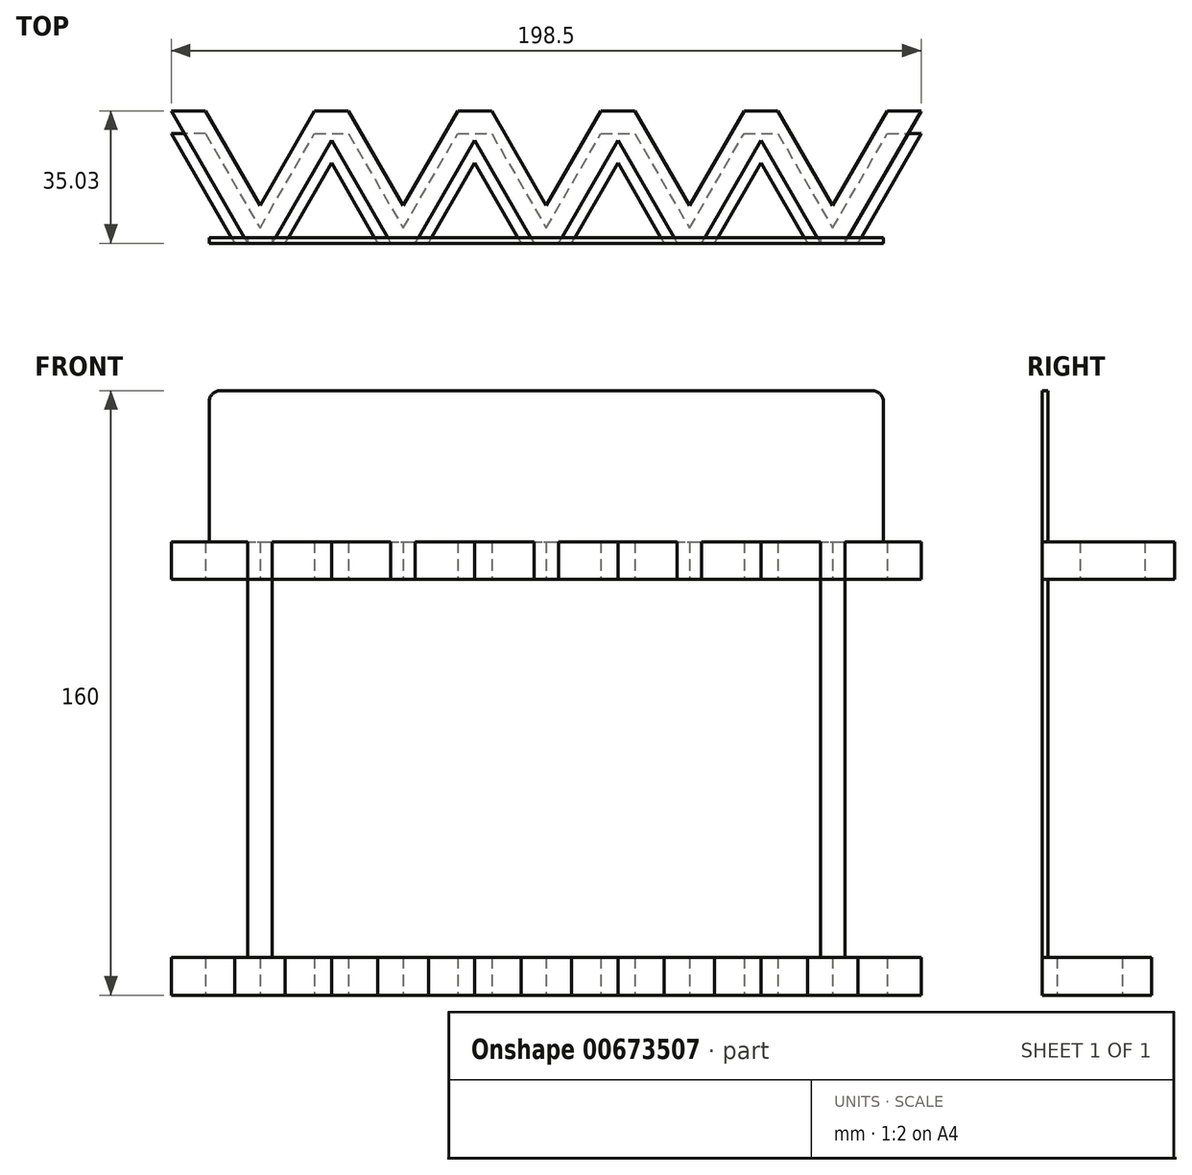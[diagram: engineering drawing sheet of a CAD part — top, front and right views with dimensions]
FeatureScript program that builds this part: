
annotation { "Feature Type Name" : "Feature", "Feature Type Description" : "" }
export const myFeature = defineFeature(function(context is Context, id is Id, definition is map)
    precondition{}
    {
        {
            var Q0;
            Q0=qCreatedBy(makeId("Top.planeOp"),FACE);
            var sketch = newSketch(context, id + "F0", { "sketchPlane" : qUnion([Q0])});
            skLineSegment(sketch, "E0", {"start": v(-76.95, 35.03) * mm, "end": v(-56.72, 0) * mm});
            skLineSegment(sketch, "E1", {"start": v(-50.27, 0) * mm, "end": v(-30.05, 35.03) * mm});
            skLineSegment(sketch, "E2", {"start": v(-67.95, 35.03) * mm, "end": v(-53.5, 10) * mm});
            skLineSegment(sketch, "E3", {"start": v(-53.5, 10) * mm, "end": v(-39.05, 35.03) * mm});
            skLineSegment(sketch, "E4", {"start": v(-76.95, 35.03) * mm, "end": v(-67.95, 35.03) * mm});
            skLineSegment(sketch, "E5", {"start": v(-56.72, 0) * mm, "end": v(-50.27, 0) * mm});
            skLineSegment(sketch, "E6", {"start": v(-39.05, 35.03) * mm, "end": v(-30.05, 35.03) * mm});
            skLineSegment(sketch, "E7.1.0.1", {"start": v(-39.05, 35.03) * mm, "end": v(-18.82, 0) * mm});
            skLineSegment(sketch, "E7.1.0.2", {"start": v(-30.05, 35.03) * mm, "end": v(-15.6, 10) * mm});
            skLineSegment(sketch, "E7.1.0.3", {"start": v(-15.6, 10) * mm, "end": v(-1.15, 35.03) * mm});
            skLineSegment(sketch, "E7.1.0.4", {"start": v(-1.15, 35.03) * mm, "end": v(7.85, 35.03) * mm});
            skLineSegment(sketch, "E7.1.0.5", {"start": v(-12.37, 0) * mm, "end": v(7.85, 35.03) * mm});
            skLineSegment(sketch, "E7.1.0.6", {"start": v(-18.82, 0) * mm, "end": v(-12.37, 0) * mm});
            skLineSegment(sketch, "E7.2.0.0", {"start": v(-1.15, 35.03) * mm, "end": v(7.85, 35.03) * mm});
            skLineSegment(sketch, "E7.2.0.1", {"start": v(-1.15, 35.03) * mm, "end": v(19.08, 0) * mm});
            skLineSegment(sketch, "E7.2.0.2", {"start": v(7.85, 35.03) * mm, "end": v(22.3, 10) * mm});
            skLineSegment(sketch, "E7.2.0.3", {"start": v(22.3, 10) * mm, "end": v(36.75, 35.03) * mm});
            skLineSegment(sketch, "E7.2.0.4", {"start": v(36.75, 35.03) * mm, "end": v(45.75, 35.03) * mm});
            skLineSegment(sketch, "E7.2.0.5", {"start": v(25.53, 0) * mm, "end": v(45.75, 35.03) * mm});
            skLineSegment(sketch, "E7.2.0.6", {"start": v(19.08, 0) * mm, "end": v(25.53, 0) * mm});
            skLineSegment(sketch, "E7.3.0.0", {"start": v(36.75, 35.03) * mm, "end": v(45.75, 35.03) * mm});
            skLineSegment(sketch, "E7.3.0.1", {"start": v(36.75, 35.03) * mm, "end": v(56.98, 0) * mm});
            skLineSegment(sketch, "E7.3.0.2", {"start": v(45.75, 35.03) * mm, "end": v(60.2, 10) * mm});
            skLineSegment(sketch, "E7.3.0.3", {"start": v(60.2, 10) * mm, "end": v(74.65, 35.03) * mm});
            skLineSegment(sketch, "E7.3.0.4", {"start": v(74.65, 35.03) * mm, "end": v(83.65, 35.03) * mm});
            skLineSegment(sketch, "E7.3.0.5", {"start": v(63.43, 0) * mm, "end": v(83.65, 35.03) * mm});
            skLineSegment(sketch, "E7.3.0.6", {"start": v(56.98, 0) * mm, "end": v(63.43, 0) * mm});
            skLineSegment(sketch, "E7.4.0.0", {"start": v(74.65, 35.03) * mm, "end": v(83.65, 35.03) * mm});
            skLineSegment(sketch, "E7.4.0.1", {"start": v(74.65, 35.03) * mm, "end": v(94.88, 0) * mm});
            skLineSegment(sketch, "E7.4.0.2", {"start": v(83.65, 35.03) * mm, "end": v(98.1, 10) * mm});
            skLineSegment(sketch, "E7.4.0.3", {"start": v(98.1, 10) * mm, "end": v(112.55, 35.03) * mm});
            skLineSegment(sketch, "E7.4.0.4", {"start": v(112.55, 35.03) * mm, "end": v(121.55, 35.03) * mm});
            skLineSegment(sketch, "E7.4.0.5", {"start": v(101.33, 0) * mm, "end": v(121.55, 35.03) * mm});
            skLineSegment(sketch, "E7.4.0.6", {"start": v(94.88, 0) * mm, "end": v(101.33, 0) * mm});
            skLineSegment(sketch, "E7.direction1", {"start": v(-76.95, 35.03) * mm, "end": v(-39.05, 35.03) * mm, "construction": true});
            skSolve(sketch);
        }
        {
            var Q0;
            Q0 = qSketchRegion(id + "F0", true);
            extrude(context, id + "F1", {"entities" : qUnion([Q0]), "endBound" : BoundingType.SYMMETRIC, "depth" : 10 * mm, "offsetDistance" : 25 * mm});
        }
        {
            var Q0;
            Q0=qCreatedBy(makeId("Top.planeOp"),FACE);
            cPlane(context, id + "F2", {"entities" : qUnion([Q0]), "cplaneType" : CPlaneType.OFFSET, "offset" : 110 * mm, "oppositeDirection" : true, "width" : 150 * mm, "height" : 150 * mm});
        }
        {
            var Q0;
            Q0=qCreatedBy(id+"F2.planeOp",FACE);
            var sketch = newSketch(context, id + "F3", { "sketchPlane" : qUnion([Q0])});
            skLineSegment(sketch, "E8", {"start": v(-76.95, 29.03) * mm, "end": v(-60.19, 0) * mm});
            skLineSegment(sketch, "E9", {"start": v(-46.8, 0) * mm, "end": v(-30.05, 29.03) * mm});
            skLineSegment(sketch, "E10", {"start": v(-67.95, 29.03) * mm, "end": v(-53.5, 4) * mm});
            skLineSegment(sketch, "E11", {"start": v(-53.5, 4) * mm, "end": v(-39.05, 29.03) * mm});
            skLineSegment(sketch, "E12.1.0.0", {"start": v(-39.05, 29.03) * mm, "end": v(-30.05, 29.03) * mm});
            skLineSegment(sketch, "E13", {"start": v(-67.95, 29.03) * mm, "end": v(-76.95, 29.03) * mm});
            skLineSegment(sketch, "E14", {"start": v(-46.8, 0) * mm, "end": v(-60.19, 0) * mm});
            skLineSegment(sketch, "E15.1.0.0", {"start": v(-1.15, 29.03) * mm, "end": v(7.85, 29.03) * mm});
            skLineSegment(sketch, "E15.1.0.1", {"start": v(-8.9, 0) * mm, "end": v(7.85, 29.03) * mm});
            skLineSegment(sketch, "E15.1.0.2", {"start": v(-15.6, 4) * mm, "end": v(-1.15, 29.03) * mm});
            skLineSegment(sketch, "E15.1.0.3", {"start": v(-8.9, 0) * mm, "end": v(-22.29, 0) * mm});
            skLineSegment(sketch, "E15.1.0.4", {"start": v(-39.05, 29.03) * mm, "end": v(-22.29, 0) * mm});
            skLineSegment(sketch, "E15.1.0.5", {"start": v(-30.05, 29.03) * mm, "end": v(-15.6, 4) * mm});
            skLineSegment(sketch, "E15.1.0.6", {"start": v(-30.05, 29.03) * mm, "end": v(-39.05, 29.03) * mm});
            skLineSegment(sketch, "E15.2.0.0", {"start": v(36.75, 29.03) * mm, "end": v(45.75, 29.03) * mm});
            skLineSegment(sketch, "E15.2.0.1", {"start": v(29, 0) * mm, "end": v(45.75, 29.03) * mm});
            skLineSegment(sketch, "E15.2.0.2", {"start": v(22.3, 4) * mm, "end": v(36.75, 29.03) * mm});
            skLineSegment(sketch, "E15.2.0.3", {"start": v(29, 0) * mm, "end": v(15.61, 0) * mm});
            skLineSegment(sketch, "E15.2.0.4", {"start": v(-1.15, 29.03) * mm, "end": v(15.61, 0) * mm});
            skLineSegment(sketch, "E15.2.0.5", {"start": v(7.85, 29.03) * mm, "end": v(22.3, 4) * mm});
            skLineSegment(sketch, "E15.2.0.6", {"start": v(7.85, 29.03) * mm, "end": v(-1.15, 29.03) * mm});
            skLineSegment(sketch, "E15.3.0.0", {"start": v(74.65, 29.03) * mm, "end": v(83.65, 29.03) * mm});
            skLineSegment(sketch, "E15.3.0.1", {"start": v(66.9, 0) * mm, "end": v(83.65, 29.03) * mm});
            skLineSegment(sketch, "E15.3.0.2", {"start": v(60.2, 4) * mm, "end": v(74.65, 29.03) * mm});
            skLineSegment(sketch, "E15.3.0.3", {"start": v(66.9, 0) * mm, "end": v(53.51, 0) * mm});
            skLineSegment(sketch, "E15.3.0.4", {"start": v(36.75, 29.03) * mm, "end": v(53.51, 0) * mm});
            skLineSegment(sketch, "E15.3.0.5", {"start": v(45.75, 29.03) * mm, "end": v(60.2, 4) * mm});
            skLineSegment(sketch, "E15.3.0.6", {"start": v(45.75, 29.03) * mm, "end": v(36.75, 29.03) * mm});
            skLineSegment(sketch, "E15.4.0.0", {"start": v(112.55, 29.03) * mm, "end": v(121.55, 29.03) * mm});
            skLineSegment(sketch, "E15.4.0.1", {"start": v(104.8, 0) * mm, "end": v(121.55, 29.03) * mm});
            skLineSegment(sketch, "E15.4.0.2", {"start": v(98.1, 4) * mm, "end": v(112.55, 29.03) * mm});
            skLineSegment(sketch, "E15.4.0.3", {"start": v(104.8, 0) * mm, "end": v(91.41, 0) * mm});
            skLineSegment(sketch, "E15.4.0.4", {"start": v(74.65, 29.03) * mm, "end": v(91.41, 0) * mm});
            skLineSegment(sketch, "E15.4.0.5", {"start": v(83.65, 29.03) * mm, "end": v(98.1, 4) * mm});
            skLineSegment(sketch, "E15.4.0.6", {"start": v(83.65, 29.03) * mm, "end": v(74.65, 29.03) * mm});
            skLineSegment(sketch, "E15.direction1", {"start": v(-39.05, 29.03) * mm, "end": v(-1.15, 29.03) * mm, "construction": true});
            skSolve(sketch);
        }
        {
            var Q0;
            Q0 = qSketchRegion(id + "F3", true);
            extrude(context, id + "F4", {"entities" : qUnion([Q0]), "endBound" : BoundingType.SYMMETRIC, "depth" : 10 * mm, "offsetDistance" : 25 * mm});
        }
        {
            var Q0;
            Q0=qCreatedBy(makeId("Front.planeOp"),FACE);
            var sketch = newSketch(context, id + "F5", { "sketchPlane" : qUnion([Q0])});
            skLineSegment(sketch, "E16.bottom", {"start": v(-63.95, 45) * mm, "end": v(108.55, 45) * mm});
            skLineSegment(sketch, "E16.top", {"start": v(-66.95, 5) * mm, "end": v(111.55, 5) * mm});
            skLineSegment(sketch, "E16.left", {"start": v(-66.95, 42) * mm, "end": v(-66.95, 5) * mm});
            skLineSegment(sketch, "E16.right", {"start": v(111.55, 42) * mm, "end": v(111.55, 5) * mm});
            skPoint(sketch, "E17.visualSharp", {"position": v(-66.95, 45) * mm});
            skArc(sketch, "E17.filletArc", {"start": v(-63.95, 45) * mm, "mid": v(-66.07, 44.12) * mm, "end": v(-66.95, 42) * mm});
            skPoint(sketch, "E18.visualSharp", {"position": v(111.55, 45) * mm});
            skArc(sketch, "E18.filletArc", {"start": v(111.55, 42) * mm, "mid": v(110.67, 44.12) * mm, "end": v(108.55, 45) * mm});
            skSolve(sketch);
        }
        {
            var Q0;
            Q0 = qSketchRegion(id + "F5", true);
            extrude(context, id + "F6", {"entities" : qUnion([Q0]), "operationType" : NewBodyOperationType.ADD, "oppositeDirection" : true, "depth" : 1.5 * mm, "offsetDistance" : 25 * mm});
        }
        {
            var Q0;
            Q0=makeQuery(id+"F1.opExtrude","CAP_FACE",FACE,{"disambiguationData":[OSD([sQuery(id+"F0.wireOp",EDGE,"E0"),sQuery(id+"F0.wireOp",EDGE,"E1"),sQuery(id+"F0.wireOp",EDGE,"E2"),sQuery(id+"F0.wireOp",EDGE,"E3"),sQuery(id+"F0.wireOp",EDGE,"E4"),sQuery(id+"F0.wireOp",EDGE,"E5"),sQuery(id+"F0.wireOp",EDGE,"E6"),sQuery(id+"F0.wireOp",EDGE,"E6"),sQuery(id+"F0.wireOp",EDGE,"E7.1.0.1"),sQuery(id+"F0.wireOp",EDGE,"E7.1.0.2"),sQuery(id+"F0.wireOp",EDGE,"E7.1.0.3"),sQuery(id+"F0.wireOp",EDGE,"E7.1.0.4"),sQuery(id+"F0.wireOp",EDGE,"E7.1.0.5"),sQuery(id+"F0.wireOp",EDGE,"E7.1.0.6"),sQuery(id+"F0.wireOp",EDGE,"E7.2.0.0"),sQuery(id+"F0.wireOp",EDGE,"E7.2.0.1"),sQuery(id+"F0.wireOp",EDGE,"E7.2.0.2"),sQuery(id+"F0.wireOp",EDGE,"E7.2.0.3"),sQuery(id+"F0.wireOp",EDGE,"E7.2.0.4"),sQuery(id+"F0.wireOp",EDGE,"E7.2.0.5"),sQuery(id+"F0.wireOp",EDGE,"E7.2.0.6"),sQuery(id+"F0.wireOp",EDGE,"E7.3.0.0"),sQuery(id+"F0.wireOp",EDGE,"E7.3.0.1"),sQuery(id+"F0.wireOp",EDGE,"E7.3.0.2"),sQuery(id+"F0.wireOp",EDGE,"E7.3.0.3"),sQuery(id+"F0.wireOp",EDGE,"E7.3.0.4"),sQuery(id+"F0.wireOp",EDGE,"E7.3.0.5"),sQuery(id+"F0.wireOp",EDGE,"E7.3.0.6"),sQuery(id+"F0.wireOp",EDGE,"E7.4.0.0"),sQuery(id+"F0.wireOp",EDGE,"E7.4.0.1"),sQuery(id+"F0.wireOp",EDGE,"E7.4.0.2"),sQuery(id+"F0.wireOp",EDGE,"E7.4.0.3"),sQuery(id+"F0.wireOp",EDGE,"E7.4.0.4"),sQuery(id+"F0.wireOp",EDGE,"E7.4.0.5"),sQuery(id+"F0.wireOp",EDGE,"E7.4.0.6")])],"isStart":true});
            var sketch = newSketch(context, id + "F7", { "sketchPlane" : qUnion([Q0])});
            skLineSegment(sketch, "E19.bottom", {"start": v(101.33, 0) * mm, "end": v(94.88, 0) * mm});
            skLineSegment(sketch, "E19.top", {"start": v(101.33, -1.5) * mm, "end": v(94.88, -1.5) * mm});
            skLineSegment(sketch, "E19.left", {"start": v(101.33, 0) * mm, "end": v(101.33, -1.5) * mm});
            skLineSegment(sketch, "E19.right", {"start": v(94.88, 0) * mm, "end": v(94.88, -1.5) * mm});
            skLineSegment(sketch, "E20.bottom", {"start": v(-50.27, 0) * mm, "end": v(-56.72, 0) * mm});
            skLineSegment(sketch, "E20.top", {"start": v(-50.27, -1.5) * mm, "end": v(-56.72, -1.5) * mm});
            skLineSegment(sketch, "E20.left", {"start": v(-50.27, 0) * mm, "end": v(-50.27, -1.5) * mm});
            skLineSegment(sketch, "E20.right", {"start": v(-56.72, 0) * mm, "end": v(-56.72, -1.5) * mm});
            skSolve(sketch);
        }
        {
            var Q0;
            Q0 = qSketchRegion(id + "F7", true);
            extrude(context, id + "F8", {"entities" : qUnion([Q0]), "endBound" : BoundingType.UP_TO_NEXT, "depth" : 25 * mm, "offsetDistance" : 25 * mm});
        }
    });
